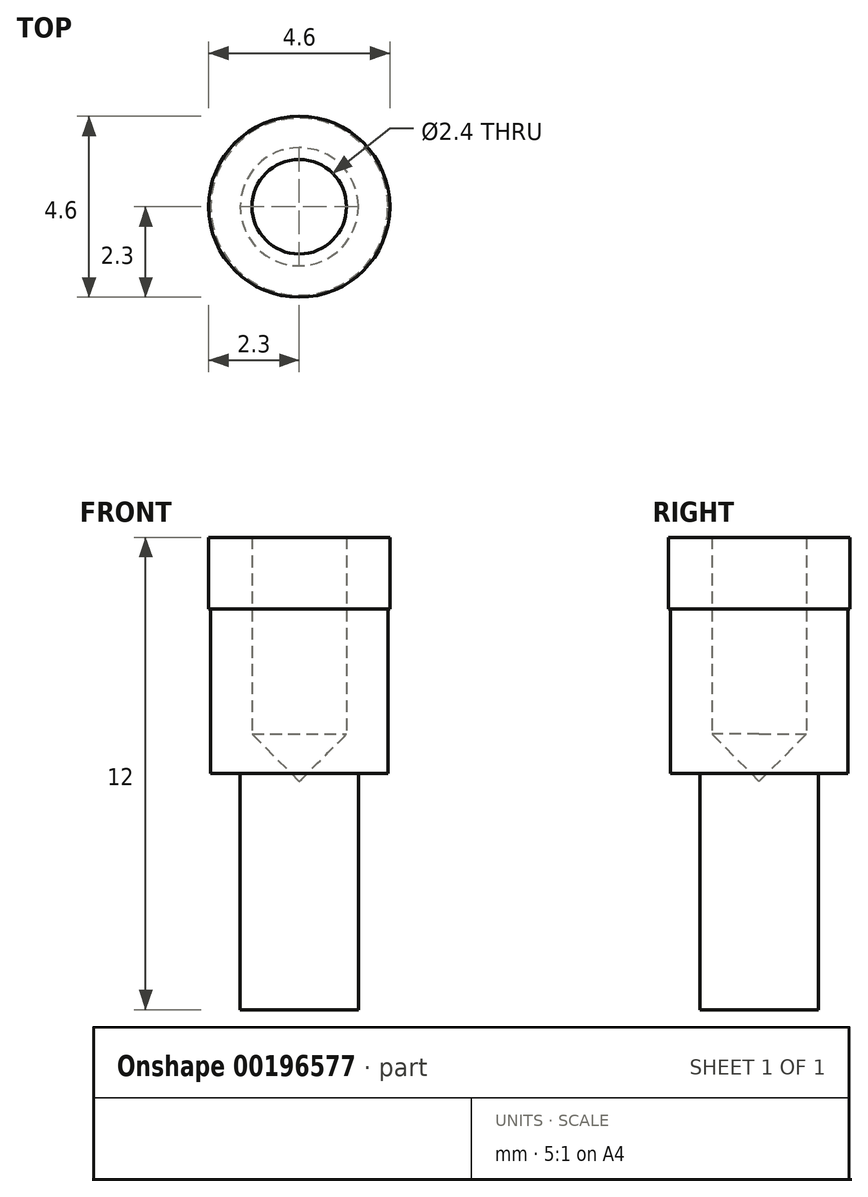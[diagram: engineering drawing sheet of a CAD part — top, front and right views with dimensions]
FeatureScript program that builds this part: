
annotation { "Feature Type Name" : "Feature", "Feature Type Description" : "" }
export const myFeature = defineFeature(function(context is Context, id is Id, definition is map)
    precondition{}
    {
        {
            var Q0;
            Q0=qCreatedBy(makeId("Front.planeOp"),FACE);
            var sketch = newSketch(context, id + "F0", { "sketchPlane" : qUnion([Q0])});
            skLineSegment(sketch, "E0", {"start": v(0, 0) * mm, "end": v(0, 5.8) * mm});
            skLineSegment(sketch, "E1", {"start": v(1.2, 12) * mm, "end": v(2.3, 12) * mm});
            skLineSegment(sketch, "E2", {"start": v(2.3, 12) * mm, "end": v(2.3, 10.19) * mm});
            skLineSegment(sketch, "E3", {"start": v(2.3, 10.19) * mm, "end": v(2.25, 10.19) * mm});
            skLineSegment(sketch, "E4", {"start": v(2.25, 10.19) * mm, "end": v(2.25, 6) * mm});
            skLineSegment(sketch, "E5", {"start": v(2.25, 6) * mm, "end": v(1.5, 6) * mm});
            skLineSegment(sketch, "E6", {"start": v(1.5, 6) * mm, "end": v(1.5, 0) * mm});
            skLineSegment(sketch, "E7", {"start": v(1.5, 0) * mm, "end": v(0, 0) * mm});
            skLineSegment(sketch, "E8", {"start": v(1.2, 12) * mm, "end": v(1.2, 7) * mm});
            skLineSegment(sketch, "E9", {"start": v(1.2, 7) * mm, "end": v(0, 5.8) * mm});
            skLineSegment(sketch, "E10", {"start": v(0, 0) * mm, "end": v(0, 14.42) * mm, "construction": true});
            skSolve(sketch);
        }
        {
            var Q0;
            Q0 = qSketchRegion(id + "F0", true);
            var Q1;
            Q1=sQuery(id+"F0.wireOp",EDGE,"E10");
            revolve(context, id + "F1", {"entities" : qUnion([Q0]), "axis" : qUnion([Q1]), "revolveType" : RevolveType.FULL});
        }
    });
